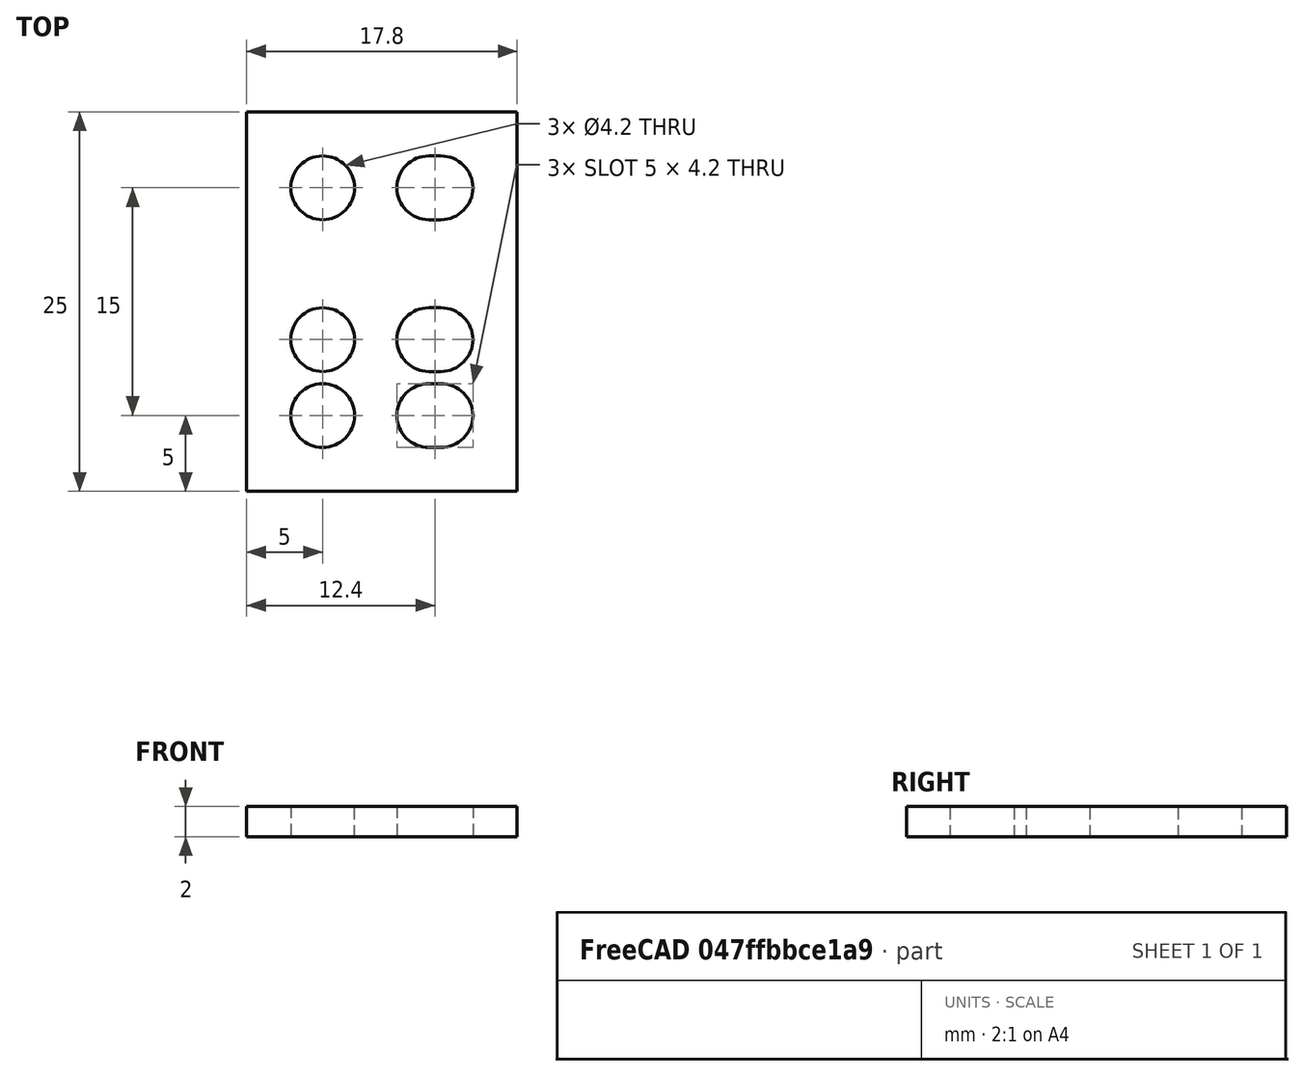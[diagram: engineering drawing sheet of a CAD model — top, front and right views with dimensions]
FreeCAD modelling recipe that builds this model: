
FCSTD DOCUMENT  (FreeCAD 0.19R24291 (Git))
Label: chain_end_holder
License: All rights reserved
LicenseURL: http://en.wikipedia.org/wiki/All_rights_reserved
objects: Sketcher::SketchObject×1, Part::Extrusion×1
note: 2 computed .brp shape members not serialized (recipe doc carries the construction recipe); baked Part::Feature solids carry a one-line shape summary decoded from their .brp

FEATURE [Sketcher::SketchObject] Sketch
  FullyConstrained = true
  sketch-geometry (21):
    g0: Circle CenterX=0 CenterY=0 CenterZ=0 NormalX=0 NormalY=0 NormalZ=1 AngleXU=0 Radius=2.1
    g1: ArcOfCircle CenterX=7 CenterY=0 CenterZ=0 NormalX=0 NormalY=0 NormalZ=1 AngleXU=0 Radius=2.1 StartAngle=1.5708 EndAngle=4.71239
    g2: ArcOfCircle CenterX=7.8 CenterY=0 CenterZ=0 NormalX=0 NormalY=0 NormalZ=1 AngleXU=0 Radius=2.1 StartAngle=4.71239 EndAngle=7.85398
    g3: LineSegment StartX=7 StartY=-2.1 StartZ=0 EndX=7.8 EndY=-2.1 EndZ=0
    g4: LineSegment StartX=7 StartY=2.1 StartZ=0 EndX=7.8 EndY=2.1 EndZ=0
    g5: LineSegment StartX=-5 StartY=5 StartZ=0 EndX=12.8 EndY=5 EndZ=0
    g6: LineSegment StartX=12.8 StartY=5 StartZ=0 EndX=12.8 EndY=-20 EndZ=0
    g7: LineSegment StartX=12.8 StartY=-20 StartZ=0 EndX=-5 EndY=-20 EndZ=0
    g8: LineSegment StartX=-5 StartY=-20 StartZ=0 EndX=-5 EndY=5 EndZ=0
    g9: Circle CenterX=0 CenterY=-15 CenterZ=0 NormalX=0 NormalY=0 NormalZ=1 AngleXU=0 Radius=2.1
    g10: ArcOfCircle CenterX=7 CenterY=-15 CenterZ=0 NormalX=0 NormalY=0 NormalZ=1 AngleXU=0 Radius=2.1 StartAngle=1.5708 EndAngle=4.71239
    g11: ArcOfCircle CenterX=7.8 CenterY=-15 CenterZ=0 NormalX=0 NormalY=0 NormalZ=1 AngleXU=0 Radius=2.1 StartAngle=4.71239 EndAngle=7.85398
    g12: LineSegment StartX=7 StartY=-17.1 StartZ=0 EndX=7.8 EndY=-17.1 EndZ=0
    g13: LineSegment StartX=7 StartY=-12.9 StartZ=0 EndX=7.8 EndY=-12.9 EndZ=0
    g14: LineSegment StartX=0 StartY=-15 StartZ=0 EndX=100 EndY=-15 EndZ=0
    g15: Circle CenterX=0 CenterY=-10 CenterZ=0 NormalX=0 NormalY=0 NormalZ=1 AngleXU=0 Radius=2.1
    g16: ArcOfCircle CenterX=7 CenterY=-10 CenterZ=0 NormalX=0 NormalY=0 NormalZ=1 AngleXU=0 Radius=2.1 StartAngle=1.5708 EndAngle=4.71239
    g17: ArcOfCircle CenterX=7.8 CenterY=-10 CenterZ=0 NormalX=0 NormalY=0 NormalZ=1 AngleXU=0 Radius=2.1 StartAngle=4.71239 EndAngle=7.85398
    g18: LineSegment StartX=7 StartY=-12.1 StartZ=0 EndX=7.8 EndY=-12.1 EndZ=0
    g19: LineSegment StartX=7 StartY=-7.9 StartZ=0 EndX=7.8 EndY=-7.9 EndZ=0
    g20: LineSegment StartX=0 StartY=-10 StartZ=0 EndX=100 EndY=-10 EndZ=0
  constraints (56):
    c: Coincident(g0,g-1)
    c: Diameter(g0) = 4.2
    c: Tangent(g1,g4) = 1.5708
    c: Tangent(g1,g3) = -1.5708
    c: Tangent(g3,g2) = -1.5708
    c: Tangent(g4,g2) = 1.5708
    c: Horizontal(g3)
    c: Equal(g1,g2)
    c: PointOnObject(g1,g-1)
    c: DistanceX(g0,g1) = 7
    c: DistanceX(g0,g2) = 7.8
    c: Diameter(g2) = 4.2
    c: Coincident(g5,g6)
    c: Coincident(g6,g7)
    c: Coincident(g7,g8)
    c: Coincident(g8,g5)
    c: Horizontal(g5)
    c: Horizontal(g7)
    c: Vertical(g6)
    c: Vertical(g8)
    c: Equal(g0,g9) = 4.2
    c: Tangent(g10,g13) = 1.5708
    c: Tangent(g10,g12) = -1.5708
    c: Tangent(g12,g11) = -1.5708
    c: Tangent(g13,g11) = 1.5708
    c: Horizontal(g12)
    c: Equal(g10,g11)
    c: DistanceX(g9,g10) = 7
    c: DistanceX(g9,g11) = 7.8
    c: Equal(g2,g11) = 4.2
    c: PointOnObject(g14,g-2)
    c: Horizontal(g14)
    c: DistanceX(g14,g14) = 100
    c: Coincident(g9,g14)
    c: PointOnObject(g10,g14)
    c: DistanceY(g9,g0) = 15
    c: DistanceY(g0,g5) = 5
    c: DistanceX(g5,g0) = 5
    c: DistanceX(g2,g5) = 5
    c: DistanceY(g6,g11) = 5
    c: Tangent(g16,g19) = 1.5708
    c: Tangent(g16,g18) = -1.5708
    c: Tangent(g18,g17) = -1.5708
    c: Tangent(g19,g17) = 1.5708
    c: Horizontal(g18)
    c: Equal(g16,g17)
    c: DistanceX(g15,g16) = 7
    c: DistanceX(g15,g17) = 7.8
    c: PointOnObject(g20,g-2)
    c: Equal(g20,g14)
    c: Horizontal(g20)
    c: Coincident(g15,g20)
    c: PointOnObject(g16,g20)
    c: DistanceY(g15,g0) = 10
    c: Equal(g17,g11)
    c: Equal(g15,g9)
FEATURE [Part::Extrusion] Extrude
  Base = -> Sketch
  Dir = (0,0,1)
  DirMode = 2
  FaceMakerClass = Part::FaceMakerBullseye
  LengthFwd = 2
  LengthRev = 0
  Solid = true
  Symmetric = false
